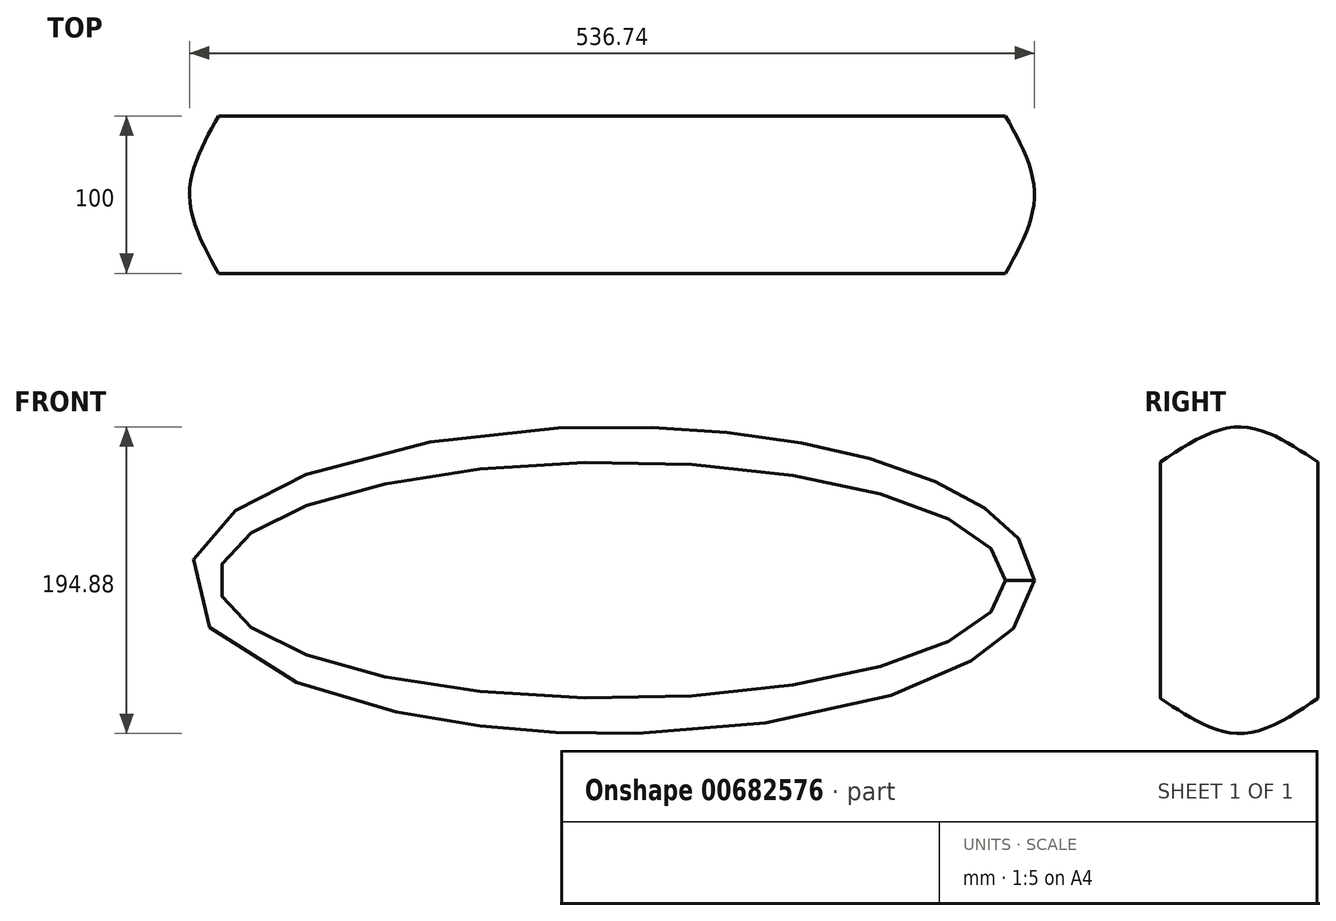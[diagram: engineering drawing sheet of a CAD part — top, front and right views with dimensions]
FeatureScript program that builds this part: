
annotation { "Feature Type Name" : "Feature", "Feature Type Description" : "" }
export const myFeature = defineFeature(function(context is Context, id is Id, definition is map)
    precondition{}
    {
        {
            var Q0;
            Q0=qCreatedBy(makeId("Front.planeOp"),FACE);
            cPlane(context, id + "F0", {"entities" : qUnion([Q0]), "cplaneType" : CPlaneType.OFFSET, "offset" : 50 * mm, "width" : 150 * mm, "height" : 150 * mm});
        }
        {
            var Q0;
            Q0=qCreatedBy(id+"F0.planeOp",FACE);
            var sketch = newSketch(context, id + "F1", { "sketchPlane" : qUnion([Q0])});
            skEllipse(sketch, "E0", {"center": v(0, 0) * mm, "majorRadius": 250 * mm, "minorRadius": 75 * mm, "majorAxis": v(1, 0)});
            skSolve(sketch);
        }
        {
            var Q0;
            Q0=qCreatedBy(makeId("Front.planeOp"),FACE);
            cPlane(context, id + "F2", {"entities" : qUnion([Q0]), "cplaneType" : CPlaneType.OFFSET, "offset" : 50 * mm, "oppositeDirection" : true, "width" : 150 * mm, "height" : 150 * mm});
        }
        {
            var Q0;
            Q0=qCreatedBy(id+"F2.planeOp",FACE);
            var sketch = newSketch(context, id + "F3", { "sketchPlane" : qUnion([Q0])});
            skEllipse(sketch, "E1", {"center": v(0, 0) * mm, "majorRadius": 250 * mm, "minorRadius": 75 * mm, "majorAxis": v(1, 0)});
            skSolve(sketch);
        }
        {
            var Q0;
            Q0=qCreatedBy(makeId("Front.planeOp"),FACE);
            var sketch = newSketch(context, id + "F4", { "sketchPlane" : qUnion([Q0])});
            skEllipse(sketch, "E2", {"center": v(0, 0) * mm, "majorRadius": 268.37 * mm, "minorRadius": 97.44 * mm, "majorAxis": v(1, 0)});
            skSolve(sketch);
        }
        {
            var Q0;
            Q0=makeQuery(id+"F3.imprint","IMPRINT",FACE,{"disambiguationData":[TD([[makeQuery(id+"F3.imprint","IMPRINT",EDGE,{"derivedFrom":sQuery(id+"F3.wireOp",EDGE,"E1")}),1.0]])]});
            var Q1;
            Q1=makeQuery(id+"F4.imprint","IMPRINT",FACE,{"disambiguationData":[TD([[makeQuery(id+"F4.imprint","IMPRINT",EDGE,{"derivedFrom":sQuery(id+"F4.wireOp",EDGE,"E2")}),1.0]])]});
            var Q2;
            Q2=makeQuery(id+"F1.imprint","IMPRINT",FACE,{"disambiguationData":[TD([[makeQuery(id+"F1.imprint","IMPRINT",EDGE,{"derivedFrom":sQuery(id+"F1.wireOp",EDGE,"E0")}),1.0]])]});
            loft(context, id + "F5", {"sheetProfilesArray" : [{ "sheetProfileEntities" : qUnion([Q0]) }, { "sheetProfileEntities" : qUnion([Q1]) }, { "sheetProfileEntities" : qUnion([Q2]) }]});
        }
    });
